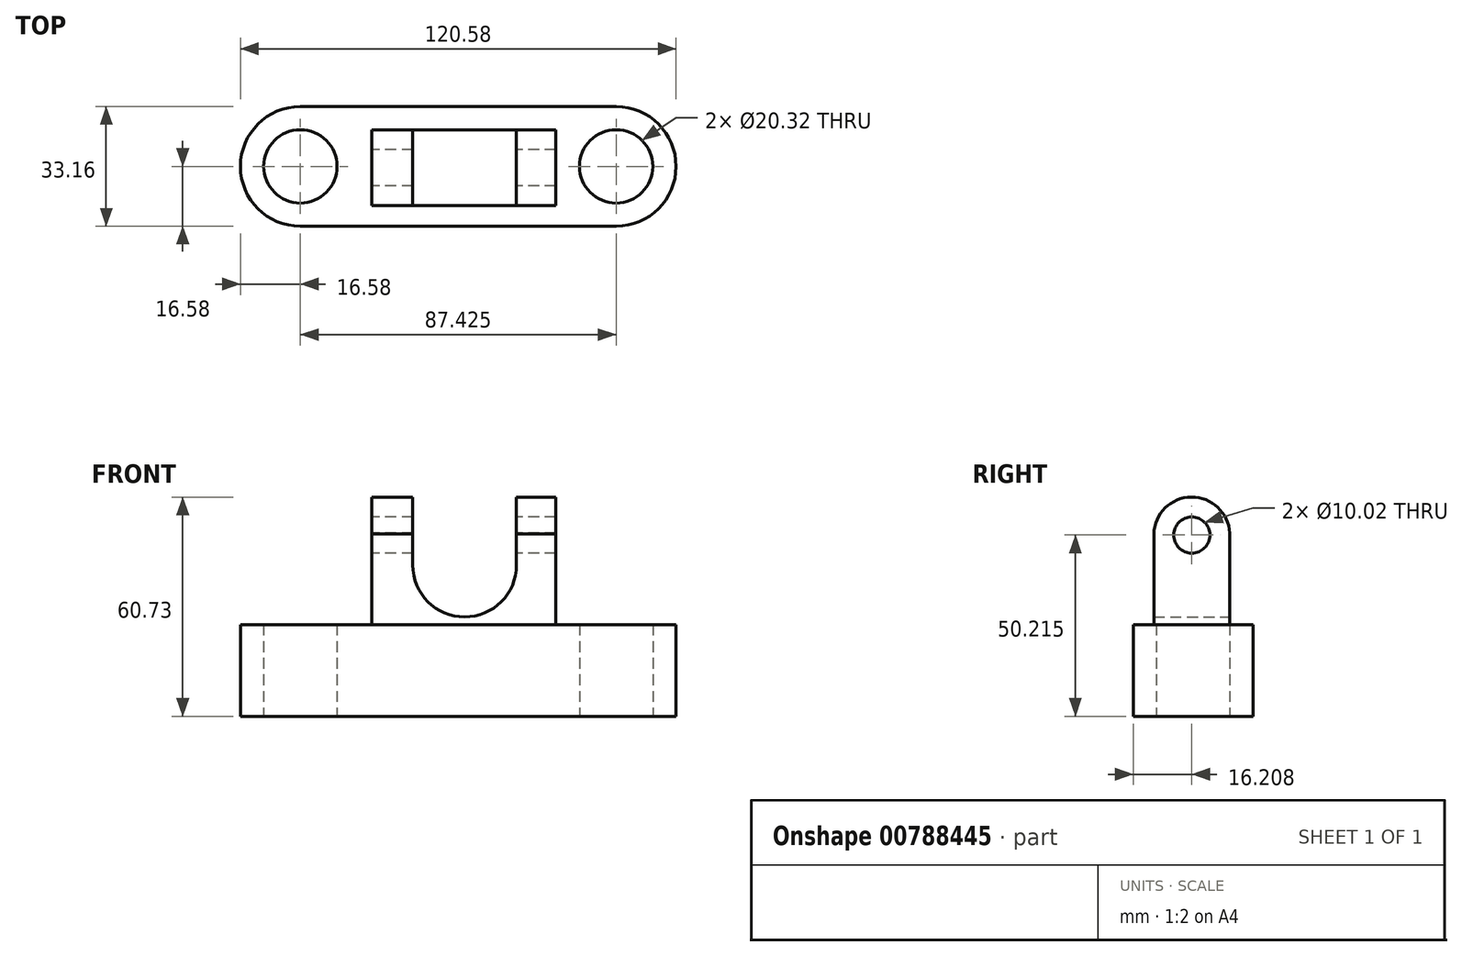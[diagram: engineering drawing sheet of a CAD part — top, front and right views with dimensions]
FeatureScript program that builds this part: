
annotation { "Feature Type Name" : "Feature", "Feature Type Description" : "" }
export const myFeature = defineFeature(function(context is Context, id is Id, definition is map)
    precondition{}
    {
        {
            var Q0;
            Q0=qCreatedBy(makeId("Top.planeOp"),FACE);
            var sketch = newSketch(context, id + "F0", { "sketchPlane" : qUnion([Q0])});
            skLineSegment(sketch, "E0.bottom", {"start": v(-45.74, 19.72) * mm, "end": v(41.68, 19.72) * mm});
            skLineSegment(sketch, "E0.top", {"start": v(-45.74, -13.44) * mm, "end": v(41.68, -13.44) * mm});
            skArc(sketch, "E1", {"start": v(-45.74, 19.72) * mm, "mid": v(-62.32, 3.14) * mm, "end": v(-45.74, -13.44) * mm});
            skArc(sketch, "E2", {"start": v(41.68, -13.44) * mm, "mid": v(58.26, 3.14) * mm, "end": v(41.68, 19.72) * mm});
            skCircle(sketch, "E3", {"center": v(-45.74, 3.14) * mm, "radius": 10.16 * mm});
            skCircle(sketch, "E4", {"center": v(41.68, 3.14) * mm, "radius": 10.16 * mm});
            skSolve(sketch);
        }
        {
            var Q0;
            Q0=makeQuery(id+"F0.imprint","IMPRINT",FACE,{"disambiguationData":[TD([[makeQuery(id+"F0.imprint","IMPRINT",EDGE,{"derivedFrom":sQuery(id+"F0.wireOp",EDGE,"E0.bottom")}),-1.0]])]});
            extrude(context, id + "F1", {"entities" : qUnion([Q0]), "depth" : 25.4 * mm, "offsetDistance" : 25.4 * mm});
        }
        {
            var Q0;
            Q0=makeQuery(id+"F1.opExtrude","CAP_FACE",FACE,{"disambiguationData":[OSD([sQuery(id+"F0.wireOp",EDGE,"E0.bottom"),sQuery(id+"F0.wireOp",EDGE,"E0.top"),sQuery(id+"F0.wireOp",EDGE,"E1"),sQuery(id+"F0.wireOp",EDGE,"E2"),sQuery(id+"F0.wireOp",EDGE,"E3"),sQuery(id+"F0.wireOp",EDGE,"E4")])],"isStart":false});
            var sketch = newSketch(context, id + "F2", { "sketchPlane" : qUnion([Q0])});
            skLineSegment(sketch, "E5.bottom", {"start": v(-25.96, 13.27) * mm, "end": v(24.97, 13.27) * mm});
            skLineSegment(sketch, "E5.top", {"start": v(-25.96, -7.75) * mm, "end": v(24.97, -7.75) * mm});
            skLineSegment(sketch, "E5.left", {"start": v(-25.96, 13.27) * mm, "end": v(-25.96, -7.75) * mm});
            skLineSegment(sketch, "E5.right", {"start": v(24.97, 13.27) * mm, "end": v(24.97, -7.75) * mm});
            skSolve(sketch);
        }
        {
            var Q0;
            Q0=makeQuery(id+"F2.imprint","IMPRINT",FACE,{"disambiguationData":[TD([[makeQuery(id+"F2.imprint","IMPRINT",EDGE,{"derivedFrom":sQuery(id+"F2.wireOp",EDGE,"E5.bottom")}),-1.0]])]});
            extrude(context, id + "F3", {"entities" : qUnion([Q0]), "operationType" : NewBodyOperationType.ADD, "depth" : 38.1 * mm, "offsetDistance" : 25.4 * mm});
        }
        {
            var Q0;
            Q0=makeQuery(id+"F3.opExtrude","SWEPT_FACE",FACE,{"disambiguationData":[OSD([sQuery(id+"F2.wireOp",EDGE,"E5.left")])]});
            var sketch = newSketch(context, id + "F4", { "sketchPlane" : qUnion([Q0])});
            skArc(sketch, "E6", {"start": v(7.75, 49.92) * mm, "mid": v(-2.35, 60.72) * mm, "end": v(-13.27, 50.75) * mm});
            skSolve(sketch);
        }
        {
            var Q0;
            Q0=makeQuery(id+"F3.opExtrude","SWEPT_FACE",FACE,{"disambiguationData":[OSD([sQuery(id+"F2.wireOp",EDGE,"E5.bottom")])]});
            var sketch = newSketch(context, id + "F5", { "sketchPlane" : qUnion([Q0])});
            skLineSegment(sketch, "E7", {"start": v(-14.1, 63.5) * mm, "end": v(-14.1, 41.92) * mm});
            skLineSegment(sketch, "E8", {"start": v(14.62, 41.92) * mm, "end": v(14.62, 63.5) * mm});
            skArc(sketch, "E9", {"start": v(-14.1, 41.92) * mm, "mid": v(0.26, 27.55) * mm, "end": v(14.62, 41.92) * mm});
            skSolve(sketch);
        }
        {
            var Q0;
            {var subQ0=sQuery(id+"F5.wireOp",EDGE,"E7");Q0=makeQuery(id+"F5.imprint","IMPRINT",FACE,{"disambiguationData":[TD([[makeQuery(id+"F5.imprint","IMPRINT",EDGE,{"derivedFrom":subQ0}),1.0]])]});}
            extrude(context, id + "F6", {"entities" : qUnion([Q0]), "operationType" : NewBodyOperationType.REMOVE, "oppositeDirection" : true, "depth" : 25.4 * mm, "offsetDistance" : 25.4 * mm});
        }
        {
            var Q0;
            {var subQ1=sQuery(id+"F2.wireOp",EDGE,"E5.left");var subQ6=makeQuery(id+"F3.opExtrude","CAP_EDGE",EDGE,{"disambiguationData":[OSD([subQ1])],"isStart":false});Q0=makeQuery(id+"F4.imprint","IMPRINT",FACE,{"disambiguationData":[TD([[makeQuery(id+"F4.imprint","IMPRINT",EDGE,{"derivedFrom":subQ6}),-1.0]])]});}
            extrude(context, id + "F7", {"entities" : qUnion([Q0]), "operationType" : NewBodyOperationType.REMOVE, "oppositeDirection" : true, "depth" : 58.42 * mm, "offsetDistance" : 25.4 * mm});
        }
        {
            var Q0;
            Q0=makeQuery(id+"F3.opExtrude","SWEPT_FACE",FACE,{"disambiguationData":[OSD([sQuery(id+"F2.wireOp",EDGE,"E5.left")])]});
            var sketch = newSketch(context, id + "F8", { "sketchPlane" : qUnion([Q0])});
            skCircle(sketch, "E10", {"center": v(-2.77, 50.21) * mm, "radius": 5.01 * mm});
            skSolve(sketch);
        }
        {
            var Q0;
            Q0=makeQuery(id+"F8.imprint","IMPRINT",FACE,{"disambiguationData":[TD([[makeQuery(id+"F8.imprint","IMPRINT",EDGE,{"derivedFrom":sQuery(id+"F8.wireOp",EDGE,"E10")}),1.0]])]});
            extrude(context, id + "F9", {"entities" : qUnion([Q0]), "operationType" : NewBodyOperationType.REMOVE, "oppositeDirection" : true, "depth" : 61.47 * mm, "offsetDistance" : 25.4 * mm});
        }
    });
